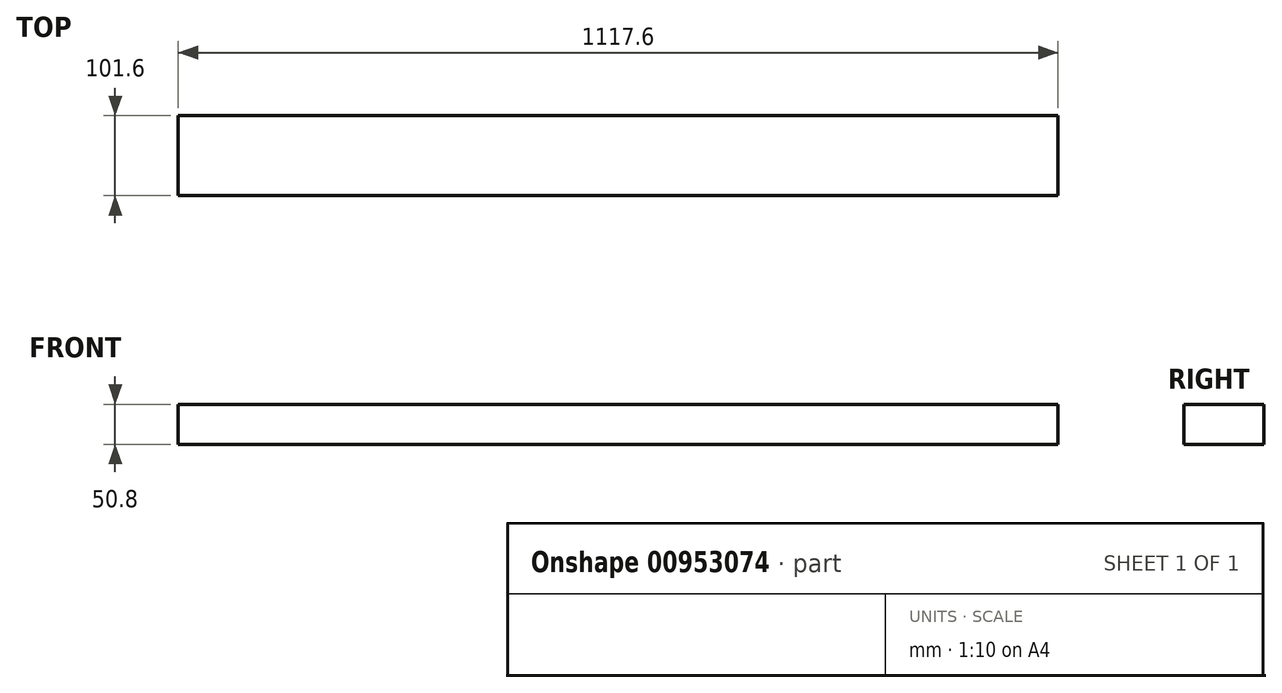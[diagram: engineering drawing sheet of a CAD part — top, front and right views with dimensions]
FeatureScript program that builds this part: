
annotation { "Feature Type Name" : "Feature", "Feature Type Description" : "" }
export const myFeature = defineFeature(function(context is Context, id is Id, definition is map)
    precondition{}
    {
        {
            var Q0;
            Q0=qCreatedBy(makeId("Top.planeOp"),FACE);
            var sketch = newSketch(context, id + "F0", { "sketchPlane" : qUnion([Q0])});
            skLineSegment(sketch, "E0", {"start": v(0, 0) * mm, "end": v(-1117.6, 0) * mm});
            skLineSegment(sketch, "E1", {"start": v(-1117.6, 0) * mm, "end": v(-1117.6, 101.6) * mm});
            skLineSegment(sketch, "E2", {"start": v(-1117.6, 101.6) * mm, "end": v(0, 101.6) * mm});
            skLineSegment(sketch, "E3", {"start": v(0, 101.6) * mm, "end": v(0, 0) * mm});
            skSolve(sketch);
        }
        {
            var Q0;
            Q0 = qSketchRegion(id + "F0", true);
            extrude(context, id + "F1", {"entities" : qUnion([Q0]), "depth" : 50.8 * mm, "offsetDistance" : 25.4 * mm});
        }
    });
